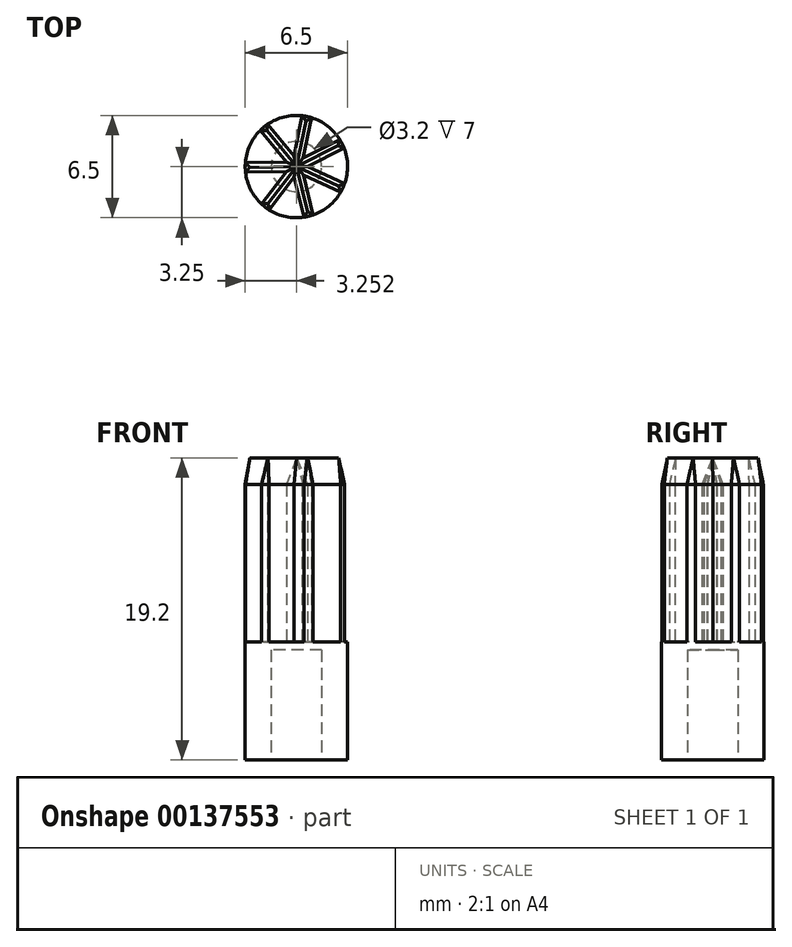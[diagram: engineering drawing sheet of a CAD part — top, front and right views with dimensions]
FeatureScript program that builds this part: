
annotation { "Feature Type Name" : "Feature", "Feature Type Description" : "" }
export const myFeature = defineFeature(function(context is Context, id is Id, definition is map)
    precondition{}
    {
        {
            var Q0;
            Q0=qCreatedBy(makeId("Top.planeOp"),FACE);
            var sketch = newSketch(context, id + "F0", { "sketchPlane" : qUnion([Q0])});
            skCircle(sketch, "E0", {"center": v(-17.52, 0) * mm, "radius": 3.25 * mm});
            skCircle(sketch, "E1", {"center": v(-17.52, 0) * mm, "radius": 1.6 * mm});
            skSolve(sketch);
        }
        {
            var Q0;
            Q0=makeQuery(id+"F0.imprint","IMPRINT",FACE,{"disambiguationData":[TD([[makeQuery(id+"F0.imprint","IMPRINT",EDGE,{"derivedFrom":sQuery(id+"F0.wireOp",EDGE,"E0")}),1.0]])]});
            var Q1;
            Q1=makeQuery(id+"F0.imprint","IMPRINT",FACE,{"disambiguationData":[TD([[makeQuery(id+"F0.imprint","IMPRINT",EDGE,{"derivedFrom":sQuery(id+"F0.wireOp",EDGE,"E1")}),1.0]])]});
            extrude(context, id + "F1", {"entities" : qUnion([Q0, Q1]), "depth" : 7.5 * mm});
        }
        {
            var Q0;
            Q0=makeQuery(id+"F1.opExtrude","CAP_FACE",FACE,{"disambiguationData":[OSD([sQuery(id+"F0.wireOp",EDGE,"E0")])],"isStart":false});
            var sketch = newSketch(context, id + "F2", { "sketchPlane" : qUnion([Q0])});
            skPoint(sketch, "E2.center", {"position": v(-17.52, 0) * mm});
            skLineSegment(sketch, "E3", {"start": v(-17.52, 0) * mm, "end": v(-20.77, -0.06) * mm});
            skLineSegment(sketch, "E4", {"start": v(-17.52, 0.3) * mm, "end": v(-20.76, 0.24) * mm});
            skLineSegment(sketch, "E5", {"start": v(-20.75, -0.36) * mm, "end": v(-17.51, -0.3) * mm});
            skLineSegment(sketch, "E6", {"start": v(-17.52, 0.3) * mm, "end": v(-17.52, 0) * mm});
            skLineSegment(sketch, "E7", {"start": v(-17.52, 0) * mm, "end": v(-17.51, -0.3) * mm});
            skLineSegment(sketch, "E8.1.0", {"start": v(-17.76, 0.18) * mm, "end": v(-19.73, -2.38) * mm});
            skLineSegment(sketch, "E8.1.1", {"start": v(-19.25, -2.75) * mm, "end": v(-17.28, -0.18) * mm});
            skLineSegment(sketch, "E8.2.0", {"start": v(-17.8, -0.07) * mm, "end": v(-17.03, -3.21) * mm});
            skLineSegment(sketch, "E8.2.1", {"start": v(-16.45, -3.07) * mm, "end": v(-17.23, 0.07) * mm});
            skLineSegment(sketch, "E8.3.0", {"start": v(-17.64, -0.27) * mm, "end": v(-14.7, -1.62) * mm});
            skLineSegment(sketch, "E8.3.1", {"start": v(-14.45, -1.08) * mm, "end": v(-17.4, 0.27) * mm});
            skLineSegment(sketch, "E8.4.0", {"start": v(-17.38, -0.27) * mm, "end": v(-14.5, 1.19) * mm});
            skLineSegment(sketch, "E8.4.1", {"start": v(-14.76, 1.72) * mm, "end": v(-17.65, 0.27) * mm});
            skLineSegment(sketch, "E8.5.0", {"start": v(-17.22, -0.06) * mm, "end": v(-16.56, 3.1) * mm});
            skLineSegment(sketch, "E8.5.1", {"start": v(-17.15, 3.23) * mm, "end": v(-17.81, 0.06) * mm});
            skLineSegment(sketch, "E8.6.0", {"start": v(-17.29, 0.2) * mm, "end": v(-19.35, 2.68) * mm});
            skLineSegment(sketch, "E8.6.1", {"start": v(-19.81, 2.3) * mm, "end": v(-17.75, -0.2) * mm});
            skSolve(sketch);
        }
        {
            var Q0;
            Q0=makeQuery(id+"F0.imprint","IMPRINT",FACE,{"disambiguationData":[TD([[makeQuery(id+"F0.imprint","IMPRINT",EDGE,{"derivedFrom":sQuery(id+"F0.wireOp",EDGE,"E1")}),1.0]])]});
            var Q1;
            Q1=makeQuery(id+"F1.opExtrude","CAP_FACE",FACE,{"disambiguationData":[OSD([sQuery(id+"F0.wireOp",EDGE,"E0")])],"isStart":false});
            extrude(context, id + "F3", {"entities" : qUnion([Q0]), "operationType" : NewBodyOperationType.REMOVE, "endBoundEntityFace" : qUnion([Q1]), "depth" : 7 * mm});
        }
        {
            var Q0;
            {var subQ4=sQuery(id+"F2.wireOp",EDGE,"E6");Q0=makeQuery(id+"F2.imprint","IMPRINT",FACE,{"disambiguationData":[TD([[makeQuery(id+"F2.imprint","IMPRINT",EDGE,{"derivedFrom":subQ4}),-1.0]])]});}
            var Q1;
            {var subQ19=sQuery(id+"F2.wireOp",EDGE,"E6");Q1=makeQuery(id+"F2.imprint","IMPRINT",FACE,{"disambiguationData":[TD([[makeQuery(id+"F2.imprint","IMPRINT",EDGE,{"derivedFrom":subQ19}),1.0]])]});}
            var Q2;
            {var subQ0=sQuery(id+"F2.wireOp",EDGE,"E7");Q2=makeQuery(id+"F2.imprint","IMPRINT",FACE,{"disambiguationData":[TD([[makeQuery(id+"F2.imprint","IMPRINT",EDGE,{"derivedFrom":subQ0}),-1.0]])]});}
            var Q3;
            {var subQ0=sQuery(id+"F2.wireOp",EDGE,"E8.3.0");var subQ1=sQuery(id+"F2.wireOp",EDGE,"E5");var subQ2=makeQuery(id+"F2.imprint","INTERSECT",VERTEX,{"derivedFrom":[subQ1,subQ0]});Q3=makeQuery(id+"F2.imprint","IMPRINT",FACE,{"disambiguationData":[TD([[makeQuery(id+"F2.imprint","IMPRINT",EDGE,{"disambiguationData":[TD([[subQ2,1.0]])],"derivedFrom":subQ1}),-1.0]])]});}
            var Q4;
            {var subQ0=sQuery(id+"F2.wireOp",EDGE,"E8.4.0");var subQ1=sQuery(id+"F2.wireOp",EDGE,"E8.1.1");var subQ2=makeQuery(id+"F2.imprint","INTERSECT",VERTEX,{"derivedFrom":[subQ1,subQ0]});Q4=makeQuery(id+"F2.imprint","IMPRINT",FACE,{"disambiguationData":[TD([[makeQuery(id+"F2.imprint","IMPRINT",EDGE,{"disambiguationData":[TD([[subQ2,1.0]])],"derivedFrom":subQ1}),-1.0]])]});}
            var Q5;
            {var subQ0=sQuery(id+"F2.wireOp",EDGE,"E8.5.0");var subQ1=sQuery(id+"F2.wireOp",EDGE,"E8.2.1");var subQ2=makeQuery(id+"F2.imprint","INTERSECT",VERTEX,{"derivedFrom":[subQ1,subQ0]});Q5=makeQuery(id+"F2.imprint","IMPRINT",FACE,{"disambiguationData":[TD([[makeQuery(id+"F2.imprint","IMPRINT",EDGE,{"disambiguationData":[TD([[subQ2,1.0]])],"derivedFrom":subQ1}),-1.0]])]});}
            var Q6;
            {var subQ0=sQuery(id+"F2.wireOp",EDGE,"E8.6.0");var subQ1=sQuery(id+"F2.wireOp",EDGE,"E8.3.1");var subQ2=makeQuery(id+"F2.imprint","INTERSECT",VERTEX,{"derivedFrom":[subQ1,subQ0]});Q6=makeQuery(id+"F2.imprint","IMPRINT",FACE,{"disambiguationData":[TD([[makeQuery(id+"F2.imprint","IMPRINT",EDGE,{"disambiguationData":[TD([[subQ2,1.0]])],"derivedFrom":subQ1}),-1.0]])]});}
            var Q7;
            {var subQ0=sQuery(id+"F2.wireOp",EDGE,"E8.4.1");var subQ1=sQuery(id+"F2.wireOp",EDGE,"E4");var subQ2=makeQuery(id+"F2.imprint","INTERSECT",VERTEX,{"derivedFrom":[subQ1,subQ0]});Q7=makeQuery(id+"F2.imprint","IMPRINT",FACE,{"disambiguationData":[TD([[makeQuery(id+"F2.imprint","IMPRINT",EDGE,{"disambiguationData":[TD([[subQ2,-1.0]])],"derivedFrom":subQ1}),-1.0]])]});}
            var Q8;
            {var subQ0=sQuery(id+"F2.wireOp",EDGE,"E8.5.1");var subQ1=sQuery(id+"F2.wireOp",EDGE,"E4");var subQ2=makeQuery(id+"F2.imprint","INTERSECT",VERTEX,{"derivedFrom":[subQ1,subQ0]});Q8=makeQuery(id+"F2.imprint","IMPRINT",FACE,{"disambiguationData":[TD([[makeQuery(id+"F2.imprint","IMPRINT",EDGE,{"disambiguationData":[TD([[subQ2,-1.0]])],"derivedFrom":subQ1}),1.0]])]});}
            var Q9;
            {var subQ0=sQuery(id+"F2.wireOp",EDGE,"E8.1.0");var subQ1=sQuery(id+"F2.wireOp",EDGE,"E5");var subQ2=makeQuery(id+"F2.imprint","INTERSECT",VERTEX,{"derivedFrom":[subQ1,subQ0]});Q9=makeQuery(id+"F2.imprint","IMPRINT",FACE,{"disambiguationData":[TD([[makeQuery(id+"F2.imprint","IMPRINT",EDGE,{"disambiguationData":[TD([[subQ2,-1.0]])],"derivedFrom":subQ1}),1.0]])]});}
            var Q10;
            {var subQ1=sQuery(id+"F2.wireOp",EDGE,"E8.1.1");var subQ5=sQuery(id+"F2.wireOp",EDGE,"E8.2.0");var subQ8=makeQuery(id+"F2.imprint","INTERSECT",VERTEX,{"derivedFrom":[subQ1,subQ5]});Q10=makeQuery(id+"F2.imprint","IMPRINT",FACE,{"disambiguationData":[TD([[makeQuery(id+"F2.imprint","IMPRINT",EDGE,{"disambiguationData":[TD([[subQ8,-1.0]])],"derivedFrom":subQ1}),-1.0]])]});}
            var Q11;
            {var subQ5=sQuery(id+"F2.wireOp",EDGE,"E5");var subQ7=sQuery(id+"F2.wireOp",EDGE,"E8.1.0");var subQ9=makeQuery(id+"F2.imprint","INTERSECT",VERTEX,{"derivedFrom":[subQ5,subQ7]});Q11=makeQuery(id+"F2.imprint","IMPRINT",FACE,{"disambiguationData":[TD([[makeQuery(id+"F2.imprint","IMPRINT",EDGE,{"disambiguationData":[TD([[subQ9,-1.0]])],"derivedFrom":subQ5}),-1.0]])]});}
            var Q12;
            {var subQ1=sQuery(id+"F2.wireOp",EDGE,"E8.2.1");var subQ5=sQuery(id+"F2.wireOp",EDGE,"E8.3.0");var subQ8=makeQuery(id+"F2.imprint","INTERSECT",VERTEX,{"derivedFrom":[subQ1,subQ5]});Q12=makeQuery(id+"F2.imprint","IMPRINT",FACE,{"disambiguationData":[TD([[makeQuery(id+"F2.imprint","IMPRINT",EDGE,{"disambiguationData":[TD([[subQ8,-1.0]])],"derivedFrom":subQ1}),-1.0]])]});}
            var Q13;
            {var subQ1=makeQuery(id+"F1.opExtrude","CAP_EDGE",EDGE,{"disambiguationData":[OSD([sQuery(id+"F0.wireOp",EDGE,"E0")])],"isStart":false});var subQ5=sQuery(id+"F2.wireOp",EDGE,"E4");var subQ7=makeQuery(id+"F2.imprint","INTERSECT",VERTEX,{"derivedFrom":[subQ1,subQ5]});Q13=makeQuery(id+"F2.imprint","IMPRINT",FACE,{"disambiguationData":[TD([[makeQuery(id+"F2.imprint","IMPRINT",EDGE,{"disambiguationData":[TD([[subQ7,1.0]])],"derivedFrom":subQ5}),1.0]])]});}
            var Q14;
            {var subQ1=makeQuery(id+"F1.opExtrude","CAP_EDGE",EDGE,{"disambiguationData":[OSD([sQuery(id+"F0.wireOp",EDGE,"E0")])],"isStart":false});var subQ5=sQuery(id+"F2.wireOp",EDGE,"E5");var subQ6=makeQuery(id+"F2.imprint","INTERSECT",VERTEX,{"derivedFrom":[subQ1,subQ5]});Q14=makeQuery(id+"F2.imprint","IMPRINT",FACE,{"disambiguationData":[TD([[makeQuery(id+"F2.imprint","IMPRINT",EDGE,{"disambiguationData":[TD([[subQ6,-1.0]])],"derivedFrom":subQ5}),1.0]])]});}
            var Q15;
            {var subQ1=sQuery(id+"F2.wireOp",EDGE,"E8.3.1");var subQ5=sQuery(id+"F2.wireOp",EDGE,"E8.4.0");var subQ8=makeQuery(id+"F2.imprint","INTERSECT",VERTEX,{"derivedFrom":[subQ1,subQ5]});Q15=makeQuery(id+"F2.imprint","IMPRINT",FACE,{"disambiguationData":[TD([[makeQuery(id+"F2.imprint","IMPRINT",EDGE,{"disambiguationData":[TD([[subQ8,-1.0]])],"derivedFrom":subQ1}),-1.0]])]});}
            var Q16;
            {var subQ1=sQuery(id+"F2.wireOp",EDGE,"E8.4.1");var subQ5=sQuery(id+"F2.wireOp",EDGE,"E8.5.0");var subQ8=makeQuery(id+"F2.imprint","INTERSECT",VERTEX,{"derivedFrom":[subQ1,subQ5]});Q16=makeQuery(id+"F2.imprint","IMPRINT",FACE,{"disambiguationData":[TD([[makeQuery(id+"F2.imprint","IMPRINT",EDGE,{"disambiguationData":[TD([[subQ8,-1.0]])],"derivedFrom":subQ1}),-1.0]])]});}
            var Q17;
            {var subQ3=sQuery(id+"F2.wireOp",EDGE,"E4");var subQ5=sQuery(id+"F2.wireOp",EDGE,"E8.5.1");var subQ6=makeQuery(id+"F2.imprint","INTERSECT",VERTEX,{"derivedFrom":[subQ3,subQ5]});Q17=makeQuery(id+"F2.imprint","IMPRINT",FACE,{"disambiguationData":[TD([[makeQuery(id+"F2.imprint","IMPRINT",EDGE,{"disambiguationData":[TD([[subQ6,-1.0]])],"derivedFrom":subQ3}),-1.0]])]});}
            extrude(context, id + "F4", {"entities" : qUnion([Q0, Q1, Q2, Q3, Q4, Q5, Q6, Q7, Q8, Q9, Q10, Q11, Q12, Q13, Q14, Q15, Q16, Q17]), "operationType" : NewBodyOperationType.ADD, "depth" : 10 * mm});
        }
        {
            var Q0;
            Q0=makeQuery(id+"F4.opExtrude","CAP_FACE",FACE,{"disambiguationData":[OSD([sQuery(id+"F0.wireOp",EDGE,"E0"),sQuery(id+"F2.wireOp",EDGE,"E4"),sQuery(id+"F2.wireOp",EDGE,"E5"),sQuery(id+"F2.wireOp",EDGE,"E8.1.0"),sQuery(id+"F2.wireOp",EDGE,"E8.1.1"),sQuery(id+"F2.wireOp",EDGE,"E8.2.0"),sQuery(id+"F2.wireOp",EDGE,"E8.2.1"),sQuery(id+"F2.wireOp",EDGE,"E8.3.0"),sQuery(id+"F2.wireOp",EDGE,"E8.3.1"),sQuery(id+"F2.wireOp",EDGE,"E8.4.0"),sQuery(id+"F2.wireOp",EDGE,"E8.4.1"),sQuery(id+"F2.wireOp",EDGE,"E8.5.0"),sQuery(id+"F2.wireOp",EDGE,"E8.5.1"),sQuery(id+"F2.wireOp",EDGE,"E8.6.0"),sQuery(id+"F2.wireOp",EDGE,"E8.6.1")])],"isStart":false});
            var sketch = newSketch(context, id + "F5", { "sketchPlane" : qUnion([Q0])});
            skPoint(sketch, "E9", {"position": v(-17.42, 0) * mm});
            skPoint(sketch, "E9.positionSnap0", {"position": v(-17.42, 1.95) * mm});
            skSolve(sketch);
        }
        {
            var Q0;
            Q0=makeQuery(id+"F4.opExtrude","CAP_EDGE",EDGE,{"disambiguationData":[OSD([sQuery(id+"F2.wireOp",EDGE,"E8.2.0")])],"isStart":false});
            cPlane(context, id + "F6", {"entities" : qUnion([Q0]), "cplaneType" : CPlaneType.LINE_ANGLE, "offset" : 5 * mm, "angle" : 90 * degree, "width" : 150 * mm, "height" : 150 * mm});
        }
        {
            var Q0;
            {var subQ6=sQuery(id+"F2.wireOp",EDGE,"E4");Q0=makeQuery(id+"F5.imprint","IMPRINT",FACE,{"disambiguationData":[TD([[makeQuery(id+"F5.imprint","IMPRINT",EDGE,{"derivedFrom":makeQuery(id+"F4.opExtrude","CAP_EDGE",EDGE,{"disambiguationData":[OSD([subQ6])],"isStart":false})}),1.0]])]});}
            extrude(context, id + "F7", {"entities" : qUnion([Q0]), "depth" : 4 * mm, "hasDraft" : true, "draftAngle" : 10 * degree, "draftPullDirection" : true});
        }
    });
